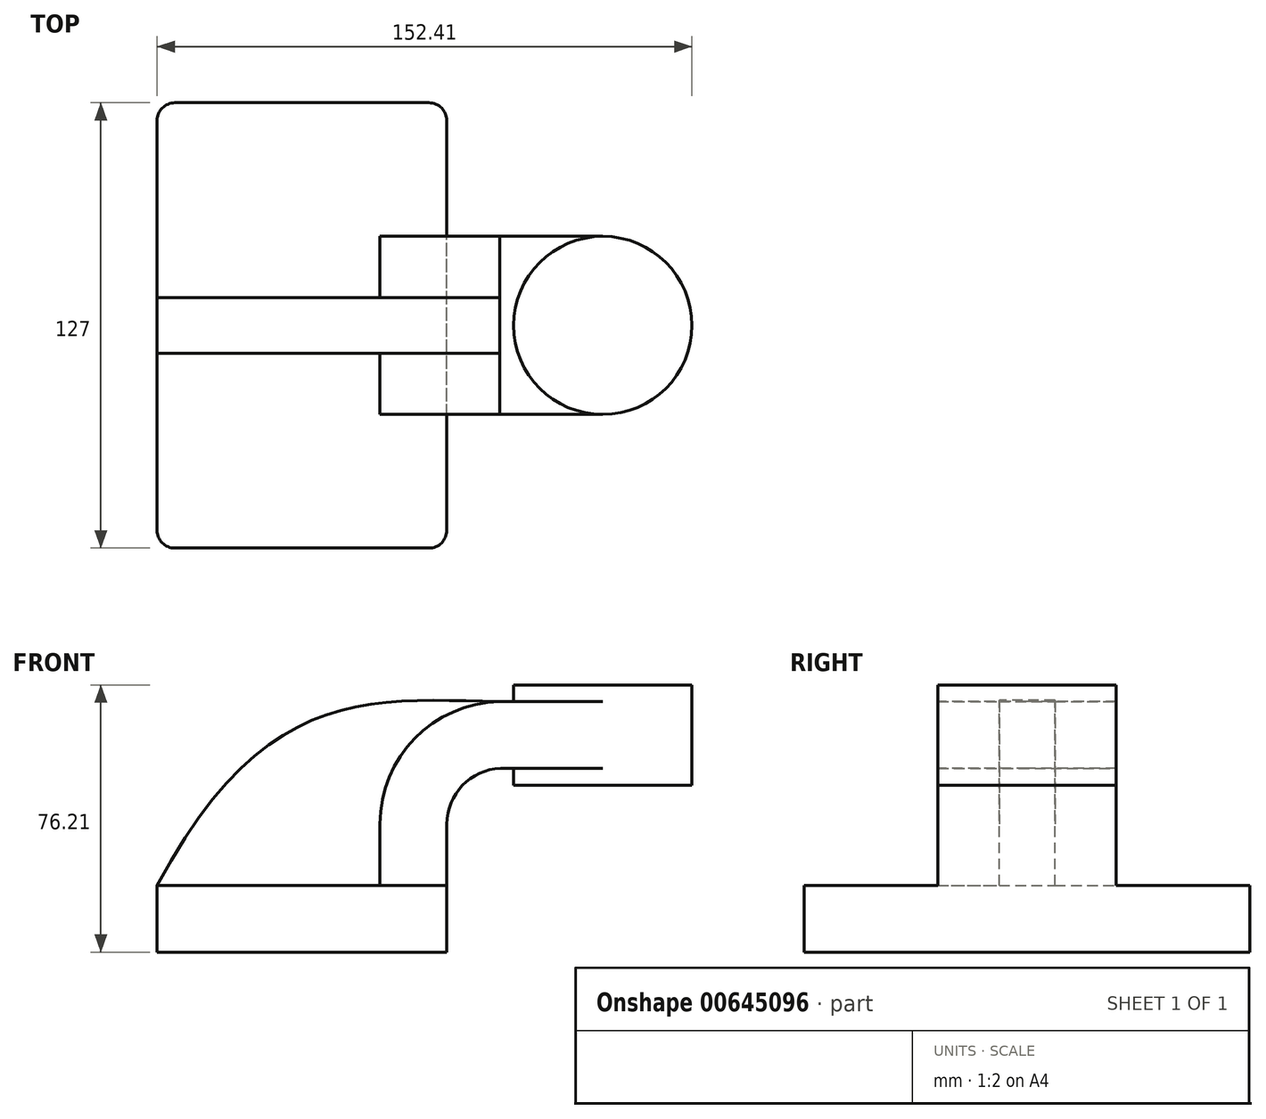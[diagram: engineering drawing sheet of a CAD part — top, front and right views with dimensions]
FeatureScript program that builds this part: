
annotation { "Feature Type Name" : "Feature", "Feature Type Description" : "" }
export const myFeature = defineFeature(function(context is Context, id is Id, definition is map)
    precondition{}
    {
        {
            var Q0;
            Q0=qCreatedBy(makeId("Front.planeOp"),FACE);
            var sketch = newSketch(context, id + "F0", { "sketchPlane" : qUnion([Q0])});
            skLineSegment(sketch, "E0.bottom", {"start": v(-41.28, 9.53) * mm, "end": v(41.28, 9.53) * mm});
            skLineSegment(sketch, "E0.top", {"start": v(-41.28, -9.53) * mm, "end": v(41.27, -9.53) * mm});
            skLineSegment(sketch, "E0.left", {"start": v(-41.28, 9.53) * mm, "end": v(-41.28, -9.52) * mm});
            skLineSegment(sketch, "E0.right", {"start": v(41.28, 9.53) * mm, "end": v(41.28, -9.52) * mm});
            skPoint(sketch, "E0.middle", {"position": v(0, 0) * mm});
            skLineSegment(sketch, "E1.bottom", {"start": v(60.32, 38.1) * mm, "end": v(111.12, 38.1) * mm});
            skLineSegment(sketch, "E1.top", {"start": v(60.32, 66.68) * mm, "end": v(111.12, 66.68) * mm});
            skLineSegment(sketch, "E1.left", {"start": v(60.32, 38.1) * mm, "end": v(60.32, 66.68) * mm});
            skLineSegment(sketch, "E1.right", {"start": v(111.13, 38.1) * mm, "end": v(111.12, 66.68) * mm});
            skPoint(sketch, "E1.middle", {"position": v(85.72, 52.39) * mm});
            skLineSegment(sketch, "E2", {"start": v(41.28, 9.52) * mm, "end": v(41.28, 27) * mm});
            skLineSegment(sketch, "E3", {"start": v(56.57, 42.86) * mm, "end": v(85.72, 42.86) * mm});
            skLineSegment(sketch, "E4.0", {"start": v(56.3, 61.9) * mm, "end": v(85.72, 61.9) * mm});
            skLineSegment(sketch, "E4.2", {"start": v(22.23, 9.52) * mm, "end": v(22.23, 27) * mm});
            skLineSegment(sketch, "E5", {"start": v(85.72, 38.1) * mm, "end": v(85.72, 66.68) * mm});
            skArc(sketch, "E6", {"start": v(41.28, 27) * mm, "mid": v(45.72, 38.01) * mm, "end": v(56.57, 42.86) * mm});
            skArc(sketch, "E7.0", {"start": v(22.23, 27) * mm, "mid": v(32.15, 51.38) * mm, "end": v(56.3, 61.9) * mm});
            skFitSpline(sketch, "E8", {"points": [v(-41.27, 9.52) * mm, v(56.3, 61.9) * mm], "startDerivative": vector(91.37, 170.97) * mm, "endDerivative": vector(112.5, -2.24) * mm});
            skSolve(sketch);
        }
        {
            var Q0;
            Q0=makeQuery(id+"F0.imprint","IMPRINT",FACE,{"disambiguationData":[TD([[makeQuery(id+"F0.imprint","IMPRINT",EDGE,{"derivedFrom":sQuery(id+"F0.wireOp",EDGE,"E0.top")}),1.0]])]});
            extrude(context, id + "F1", {"entities" : qUnion([Q0]), "endBound" : BoundingType.SYMMETRIC, "depth" : 127 * mm, "offsetDistance" : 25.4 * mm});
        }
        {
            var Q0;
            {var subQ4=sQuery(id+"F0.wireOp",EDGE,"E2");Q0=makeQuery(id+"F0.imprint","IMPRINT",FACE,{"disambiguationData":[TD([[makeQuery(id+"F0.imprint","IMPRINT",EDGE,{"derivedFrom":subQ4}),1.0]])]});}
            var Q1;
            {var subQ0=sQuery(id+"F0.wireOp",EDGE,"E3");var subQ1=sQuery(id+"F0.wireOp",EDGE,"E1.left");var subQ2=makeQuery(id+"F0.imprint","INTERSECT",VERTEX,{"derivedFrom":[subQ1,subQ0]});Q1=makeQuery(id+"F0.imprint","IMPRINT",FACE,{"disambiguationData":[TD([[makeQuery(id+"F0.imprint","IMPRINT",EDGE,{"disambiguationData":[TD([[subQ2,-1.0]])],"derivedFrom":subQ1}),-1.0]])]});}
            extrude(context, id + "F2", {"entities" : qUnion([Q0, Q1]), "operationType" : NewBodyOperationType.ADD, "endBound" : BoundingType.SYMMETRIC, "depth" : 50.8 * mm, "offsetDistance" : 25.4 * mm});
        }
        {
            var Q0;
            {var subQ2=sQuery(id+"F0.wireOp",EDGE,"E4.2");Q0=makeQuery(id+"F0.imprint","IMPRINT",FACE,{"disambiguationData":[TD([[makeQuery(id+"F0.imprint","IMPRINT",EDGE,{"derivedFrom":subQ2}),1.0]])]});}
            extrude(context, id + "F3", {"entities" : qUnion([Q0]), "operationType" : NewBodyOperationType.ADD, "endBound" : BoundingType.SYMMETRIC, "depth" : 15.88 * mm, "offsetDistance" : 25.4 * mm});
        }
        {
            var Q0;
            {var subQ4=sQuery(id+"F0.wireOp",EDGE,"E1.right");Q0=makeQuery(id+"F0.imprint","IMPRINT",FACE,{"disambiguationData":[TD([[makeQuery(id+"F0.imprint","IMPRINT",EDGE,{"derivedFrom":subQ4}),1.0]])]});}
            var Q1;
            Q1=sQuery(id+"F0.wireOp",EDGE,"E5");
            revolve(context, id + "F4", {"operationType" : NewBodyOperationType.ADD, "entities" : qUnion([Q0]), "axis" : qUnion([Q1]), "revolveType" : RevolveType.FULL});
        }
        {
            var Q0;
            Q0=makeQuery(id+"F1.opExtrude","CAP_EDGE",EDGE,{"disambiguationData":[OSD([sQuery(id+"F0.wireOp",EDGE,"E0.left")])],"isStart":false});
            var Q1;
            Q1=makeQuery(id+"F1.opExtrude","CAP_EDGE",EDGE,{"disambiguationData":[OSD([sQuery(id+"F0.wireOp",EDGE,"E0.right")])],"isStart":false});
            var Q2;
            Q2=makeQuery(id+"F1.opExtrude","CAP_EDGE",EDGE,{"disambiguationData":[OSD([sQuery(id+"F0.wireOp",EDGE,"E0.right")])],"isStart":true});
            var Q3;
            Q3=makeQuery(id+"F1.opExtrude","CAP_EDGE",EDGE,{"disambiguationData":[OSD([sQuery(id+"F0.wireOp",EDGE,"E0.left")])],"isStart":true});
            fillet(context, id + "F5", {"entities" : qUnion([Q0, Q1, Q2, Q3]), "radius" : 5.08 * mm, "tangentPropagation" : true, "allowEdgeOverflow" : false});
        }
    });
